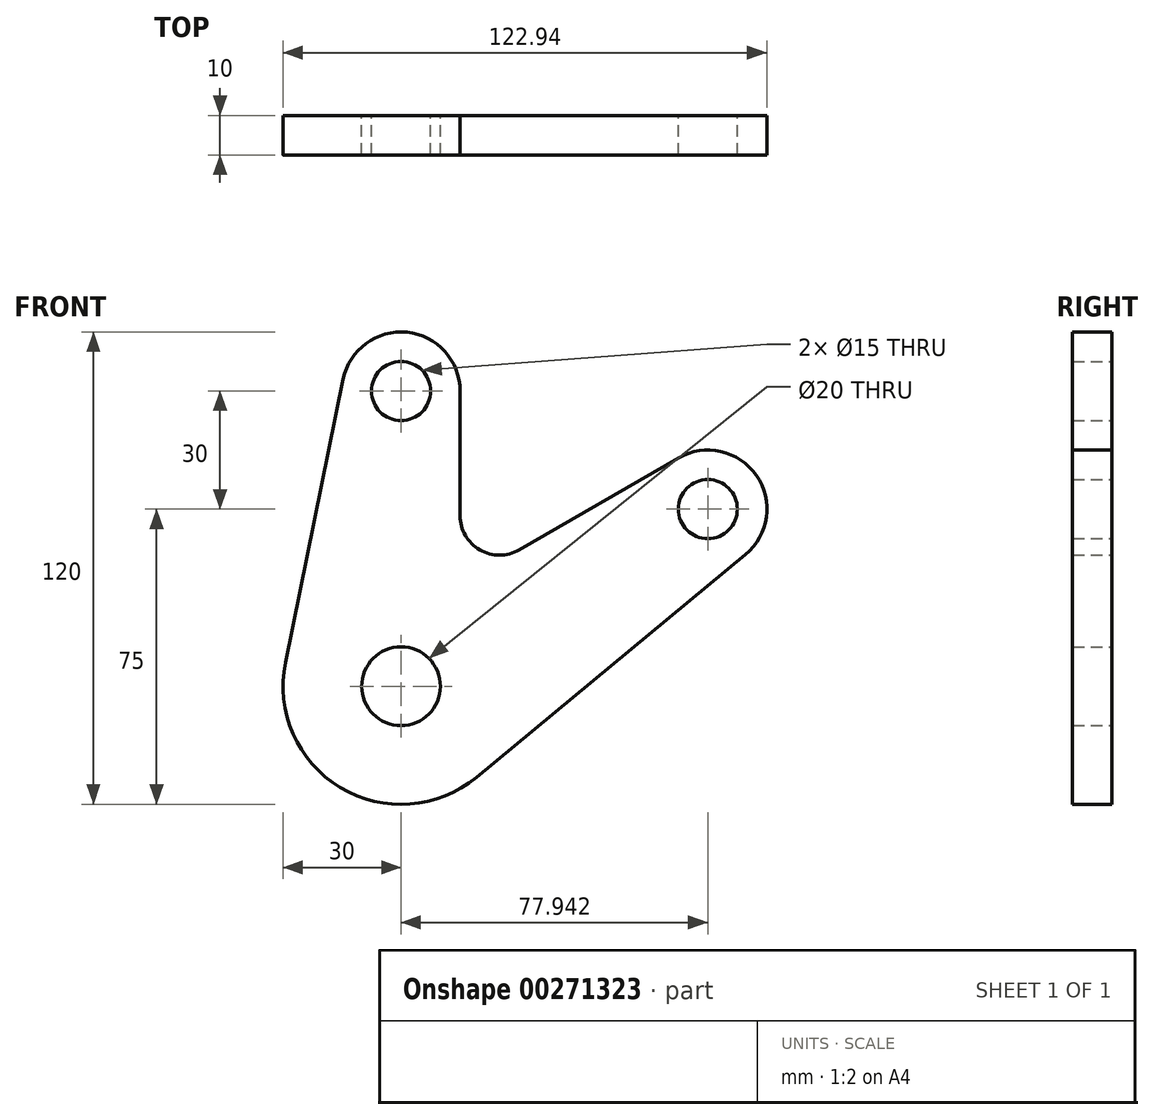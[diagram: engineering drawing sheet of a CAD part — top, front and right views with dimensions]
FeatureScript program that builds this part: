
annotation { "Feature Type Name" : "Feature", "Feature Type Description" : "" }
export const myFeature = defineFeature(function(context is Context, id is Id, definition is map)
    precondition{}
    {
        {
            var Q0;
            Q0=qCreatedBy(makeId("Front.planeOp"),FACE);
            var sketch = newSketch(context, id + "F0", { "sketchPlane" : qUnion([Q0])});
            skCircle(sketch, "E0", {"center": v(0, 0) * mm, "radius": 10 * mm});
            skCircle(sketch, "E1", {"center": v(0, 75) * mm, "radius": 7.5 * mm});
            skCircle(sketch, "E2", {"center": v(77.94, 45) * mm, "radius": 7.5 * mm});
            skArc(sketch, "E3", {"start": v(-29.4, 6) * mm, "mid": v(-15.44, -25.72) * mm, "end": v(19.12, -23.12) * mm});
            skLineSegment(sketch, "E4", {"start": v(-29.4, 6) * mm, "end": v(-14.7, 78) * mm});
            skArc(sketch, "E5", {"start": v(15, 75) * mm, "mid": v(1.5, 89.92) * mm, "end": v(-14.7, 78) * mm});
            skLineSegment(sketch, "E6", {"start": v(15, 75) * mm, "end": v(15, 43.3) * mm});
            skArc(sketch, "E7", {"start": v(15, 43.3) * mm, "mid": v(20, 34.64) * mm, "end": v(30, 34.64) * mm});
            skLineSegment(sketch, "E8", {"start": v(30, 34.64) * mm, "end": v(70.44, 58) * mm});
            skArc(sketch, "E9", {"start": v(87.5, 33.44) * mm, "mid": v(90.26, 53.56) * mm, "end": v(70.44, 58) * mm});
            skLineSegment(sketch, "E10", {"start": v(87.5, 33.44) * mm, "end": v(19.12, -23.12) * mm});
            skLineSegment(sketch, "E11", {"start": v(0, 75) * mm, "end": v(0, 0) * mm, "construction": true});
            skLineSegment(sketch, "E12", {"start": v(0, 0) * mm, "end": v(77.94, 45) * mm, "construction": true});
            skSolve(sketch);
        }
        {
            var Q0;
            Q0 = qSketchRegion(id + "F0", true);
            extrude(context, id + "F1", {"entities" : qUnion([Q0]), "depth" : 10 * mm});
        }
    });
